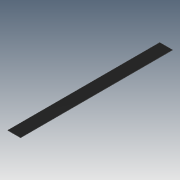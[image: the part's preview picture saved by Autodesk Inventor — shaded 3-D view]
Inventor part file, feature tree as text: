
AUTODESK INVENTOR PART (.ipt)
format: ipt  version: 2012 (Build 160160000, 160)  size: 69,120 bytes
history: native  units: in
note: dims shown in document units (in); Inventor stores cm internally (conversion verified against a paired STEP export)
features: extrude x1, sketch x1
ambient origin geometry x8: Origin, YZ Plane, XZ Plane, XY Plane, X Axis, Y Axis, Z Axis, Center Point
bodies: Solid1 (feature_tree)
feature tree (2):
  extrude  "Extrusion1"  Depth=4.0in
  sketch  "Sketch1"  dims[d6=47.5in d7=0.0in d63=4.0in d64=0.075in]
